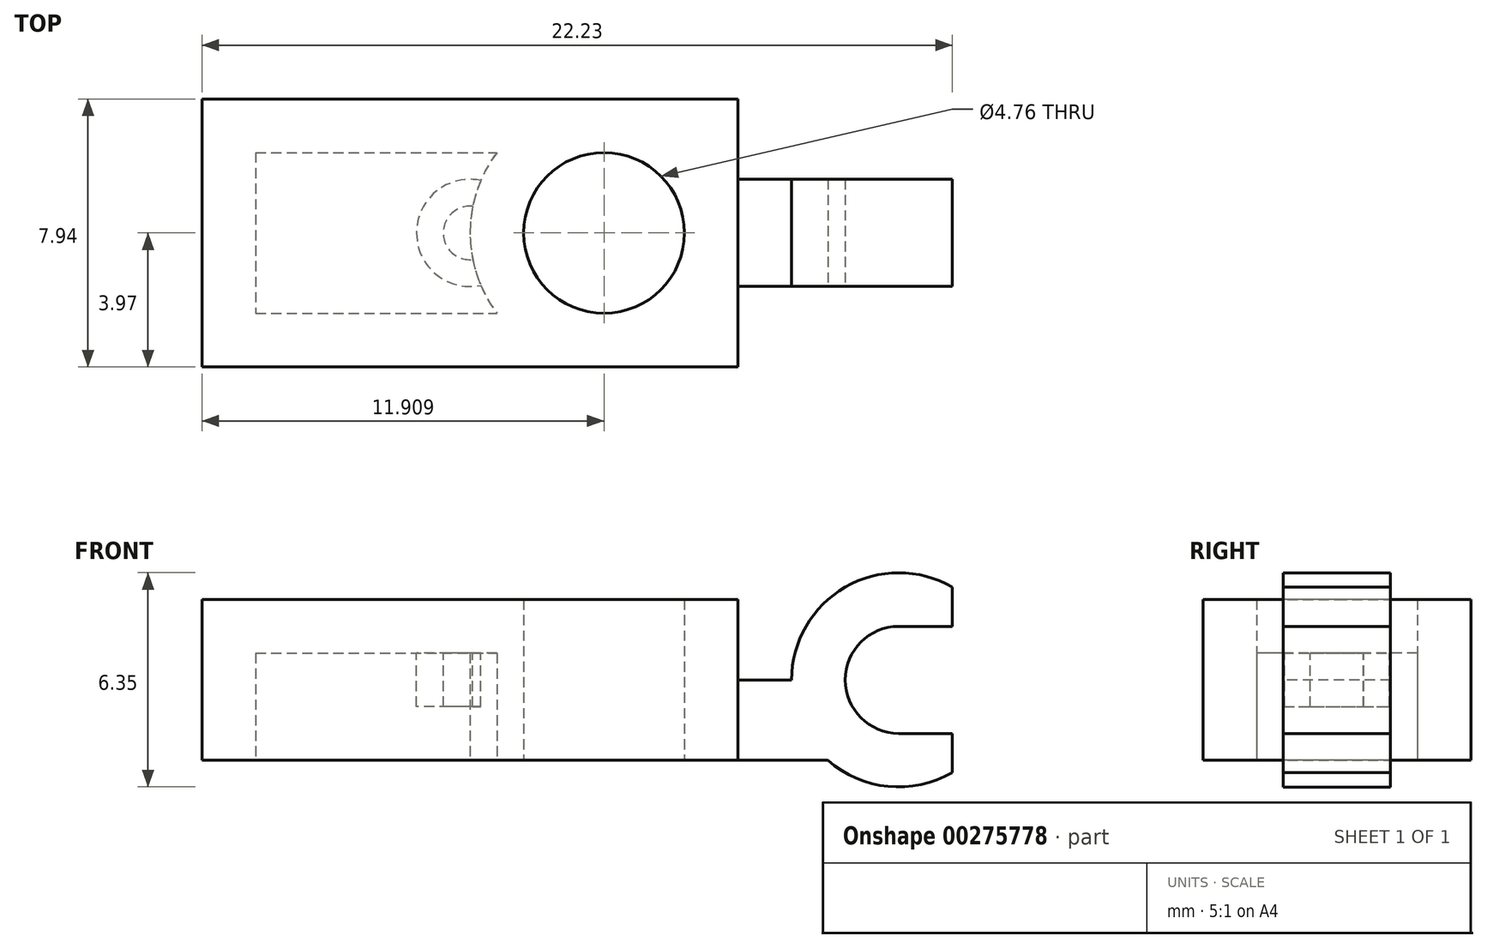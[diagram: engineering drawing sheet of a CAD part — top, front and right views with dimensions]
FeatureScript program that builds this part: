
annotation { "Feature Type Name" : "Feature", "Feature Type Description" : "" }
export const myFeature = defineFeature(function(context is Context, id is Id, definition is map)
    precondition{}
    {
        {
            var Q0;
            Q0=qCreatedBy(makeId("Top.planeOp"),FACE);
            var sketch = newSketch(context, id + "F0", { "sketchPlane" : qUnion([Q0])});
            skLineSegment(sketch, "E0.bottom", {"start": v(-7.94, 3.97) * mm, "end": v(7.94, 3.97) * mm});
            skLineSegment(sketch, "E0.top", {"start": v(-7.94, -3.97) * mm, "end": v(7.94, -3.97) * mm});
            skLineSegment(sketch, "E0.left", {"start": v(-7.94, 3.97) * mm, "end": v(-7.94, -3.97) * mm});
            skLineSegment(sketch, "E0.right", {"start": v(7.94, 3.97) * mm, "end": v(7.94, -3.97) * mm});
            skPoint(sketch, "E0.middle", {"position": v(0, 0) * mm});
            skCircle(sketch, "E1", {"center": v(-3.97, 0) * mm, "radius": 2.38 * mm});
            skCircle(sketch, "E2.MirrorC", {"center": v(3.97, 0) * mm, "radius": 2.38 * mm});
            skSolve(sketch);
        }
        {
            var Q0;
            Q0=makeQuery(id+"F0.imprint","IMPRINT",FACE,{"disambiguationData":[TD([[makeQuery(id+"F0.imprint","IMPRINT",EDGE,{"derivedFrom":sQuery(id+"F0.wireOp",EDGE,"E0.bottom")}),-1.0]])]});
            extrude(context, id + "F1", {"entities" : qUnion([Q0]), "depth" : 3.17 * mm});
        }
        {
            var Q0;
            Q0=makeQuery(id+"F0.imprint","IMPRINT",FACE,{"disambiguationData":[TD([[makeQuery(id+"F0.imprint","IMPRINT",EDGE,{"derivedFrom":sQuery(id+"F0.wireOp",EDGE,"E2.MirrorC")}),-1.0]])]});
            var Q1;
            Q1=makeQuery(id+"F0.imprint","IMPRINT",FACE,{"disambiguationData":[TD([[makeQuery(id+"F0.imprint","IMPRINT",EDGE,{"derivedFrom":sQuery(id+"F0.wireOp",EDGE,"E1")}),1.0]])]});
            extrude(context, id + "F2", {"entities" : qUnion([Q0, Q1]), "operationType" : NewBodyOperationType.ADD, "depth" : 4.76 * mm});
        }
        {
            var Q0;
            {var subQ0=sQuery(id+"F0.wireOp",EDGE,"E2.MirrorC");var subQ1=sQuery(id+"F0.wireOp",EDGE,"E1");Q0=makeQuery(id+"F2.boolean.opBoolean","MERGE",FACE,{"derivedFrom":[makeQuery(id+"F1.opExtrude","CAP_FACE",FACE,{"disambiguationData":[OSD([sQuery(id+"F0.wireOp",EDGE,"E0.bottom"),sQuery(id+"F0.wireOp",EDGE,"E0.top"),sQuery(id+"F0.wireOp",EDGE,"E0.left"),sQuery(id+"F0.wireOp",EDGE,"E0.right"),subQ1,subQ0])],"isStart":true}),makeQuery(id+"F2.opExtrude","CAP_FACE",FACE,{"disambiguationData":[OSD([subQ1])],"isStart":true}),makeQuery(id+"F2.opExtrude","CAP_FACE",FACE,{"disambiguationData":[OSD([subQ0])],"isStart":true})]});}
            shell(context, id + "F3", {"entities" : qUnion([Q0]), "thickness" : 1.59 * mm});
        }
        {
            var Q0;
            Q0=makeQuery(id+"F3.opShell","OFFSET_FACE",FACE,{"disambiguationData":[OSD([sQuery(id+"F0.wireOp",EDGE,"E0.bottom"),sQuery(id+"F0.wireOp",EDGE,"E0.top"),sQuery(id+"F0.wireOp",EDGE,"E0.left"),sQuery(id+"F0.wireOp",EDGE,"E0.right"),sQuery(id+"F0.wireOp",EDGE,"E1"),sQuery(id+"F0.wireOp",EDGE,"E2.MirrorC")])]});
            var sketch = newSketch(context, id + "F4", { "sketchPlane" : qUnion([Q0])});
            skCircle(sketch, "E3", {"center": v(0, 0) * mm, "radius": 1.59 * mm});
            skCircle(sketch, "E4", {"center": v(0, 0) * mm, "radius": 0.8 * mm});
            skSolve(sketch);
        }
        {
            var Q0;
            Q0=makeQuery(id+"F4.imprint","IMPRINT",FACE,{"disambiguationData":[TD([[makeQuery(id+"F4.imprint","IMPRINT",EDGE,{"derivedFrom":sQuery(id+"F4.wireOp",EDGE,"E3")}),1.0]])]});
            extrude(context, id + "F5", {"entities" : qUnion([Q0]), "operationType" : NewBodyOperationType.ADD, "depth" : 1.59 * mm});
        }
        {
            var Q0;
            Q0=makeQuery(id+"F1.opExtrude","SWEPT_FACE",FACE,{"disambiguationData":[OSD([sQuery(id+"F0.wireOp",EDGE,"E0.right")])]});
            var sketch = newSketch(context, id + "F6", { "sketchPlane" : qUnion([Q0])});
            skLineSegment(sketch, "E5", {"start": v(0, 0) * mm, "end": v(1.59, 0) * mm});
            skLineSegment(sketch, "E6", {"start": v(1.59, 0) * mm, "end": v(1.59, 6.35) * mm});
            skLineSegment(sketch, "E7", {"start": v(1.59, 6.35) * mm, "end": v(0, 6.35) * mm});
            skLineSegment(sketch, "E8", {"start": v(0, 6.35) * mm, "end": v(0, 0) * mm});
            skLineSegment(sketch, "E9.MirrorCS", {"start": v(-1.59, 6.35) * mm, "end": v(0, 6.35) * mm});
            skLineSegment(sketch, "E10.MirrorCS", {"start": v(-1.59, 0) * mm, "end": v(-1.59, 6.35) * mm});
            skLineSegment(sketch, "E11.MirrorCS", {"start": v(0, 0) * mm, "end": v(-1.59, 0) * mm});
            skSolve(sketch);
        }
        {
            var Q0;
            Q0=qSketchRegion(id+"F6",true);
            extrude(context, id + "F7", {"entities" : qUnion([Q0]), "operationType" : NewBodyOperationType.ADD, "depth" : 4.76 * mm});
        }
        {
            var Q0;
            Q0=makeQuery(id+"F7.opExtrude","SWEPT_FACE",FACE,{"disambiguationData":[OSD([sQuery(id+"F6.wireOp",EDGE,"E10.MirrorCS")])]});
            var sketch = newSketch(context, id + "F8", { "sketchPlane" : qUnion([Q0])});
            skLineSegment(sketch, "E12", {"start": v(7.94, 3.17) * mm, "end": v(7.94, 2.38) * mm});
            skLineSegment(sketch, "E13", {"start": v(7.94, 2.38) * mm, "end": v(9.53, 2.38) * mm});
            skLineSegment(sketch, "E14", {"start": v(9.53, 2.38) * mm, "end": v(12.7, 2.38) * mm});
            skCircle(sketch, "E15", {"center": v(12.7, 2.38) * mm, "radius": 3.17 * mm});
            skCircle(sketch, "E16.0", {"center": v(12.7, 2.38) * mm, "radius": 1.59 * mm});
            skLineSegment(sketch, "E17", {"start": v(12.7, 0) * mm, "end": v(12.7, -0.8) * mm});
            skLineSegment(sketch, "E18", {"start": v(12.7, 0) * mm, "end": v(14.29, 0) * mm});
            skLineSegment(sketch, "E19", {"start": v(14.29, 0) * mm, "end": v(14.29, -0.37) * mm});
            skLineSegment(sketch, "E20", {"start": v(14.29, -0.37) * mm, "end": v(14.29, 5.13) * mm});
            skLineSegment(sketch, "E21", {"start": v(12.7, 0.8) * mm, "end": v(14.29, 0.8) * mm});
            skLineSegment(sketch, "E22", {"start": v(12.7, 3.97) * mm, "end": v(14.29, 3.97) * mm});
            skSolve(sketch);
        }
        {
            var Q0;
            {var subQ0=sQuery(id+"F8.wireOp",EDGE,"E17");Q0=makeQuery(id+"F8.imprint","IMPRINT",FACE,{"disambiguationData":[TD([[makeQuery(id+"F8.imprint","IMPRINT",EDGE,{"derivedFrom":subQ0}),-1.0]])]});}
            var Q1;
            {var subQ0=sQuery(id+"F8.wireOp",EDGE,"E17");Q1=makeQuery(id+"F8.imprint","IMPRINT",FACE,{"disambiguationData":[TD([[makeQuery(id+"F8.imprint","IMPRINT",EDGE,{"derivedFrom":subQ0}),1.0]])]});}
            var Q2;
            {var subQ5=sQuery(id+"F8.wireOp",EDGE,"E22");Q2=makeQuery(id+"F8.imprint","IMPRINT",FACE,{"disambiguationData":[TD([[makeQuery(id+"F8.imprint","IMPRINT",EDGE,{"derivedFrom":subQ5}),1.0]])]});}
            var Q3;
            {var subQ0=sQuery(id+"F8.wireOp",EDGE,"E18");Q3=makeQuery(id+"F8.imprint","IMPRINT",FACE,{"disambiguationData":[TD([[makeQuery(id+"F8.imprint","IMPRINT",EDGE,{"derivedFrom":subQ0}),1.0]])]});}
            extrude(context, id + "F9", {"entities" : qUnion([Q0, Q1, Q2, Q3]), "operationType" : NewBodyOperationType.ADD, "oppositeDirection" : true, "depth" : 3.17 * mm});
        }
        {
            var Q0;
            Q0=makeQuery(id+"F8.imprint","IMPRINT",FACE,{"disambiguationData":[TD([[makeQuery(id+"F8.imprint","IMPRINT",EDGE,{"derivedFrom":sQuery(id+"F8.wireOp",EDGE,"E12")}),-1.0]])]});
            var Q1;
            {var subQ0=sQuery(id+"F8.wireOp",EDGE,"E14");var subQ1=makeQuery(id+"F7.opExtrude","CAP_EDGE",EDGE,{"disambiguationData":[OSD([sQuery(id+"F6.wireOp",EDGE,"E10.MirrorCS")])],"isStart":false});var subQ2=makeQuery(id+"F8.imprint","INTERSECT",VERTEX,{"derivedFrom":[subQ1,subQ0]});Q1=makeQuery(id+"F8.imprint","IMPRINT",FACE,{"disambiguationData":[TD([[makeQuery(id+"F8.imprint","IMPRINT",EDGE,{"disambiguationData":[TD([[subQ2,1.0]])],"derivedFrom":subQ0}),-1.0]])]});}
            var Q2;
            {var subQ0=sQuery(id+"F8.wireOp",EDGE,"E14");var subQ1=makeQuery(id+"F7.opExtrude","CAP_EDGE",EDGE,{"disambiguationData":[OSD([sQuery(id+"F6.wireOp",EDGE,"E10.MirrorCS")])],"isStart":false});var subQ2=makeQuery(id+"F8.imprint","INTERSECT",VERTEX,{"derivedFrom":[subQ1,subQ0]});Q2=makeQuery(id+"F8.imprint","IMPRINT",FACE,{"disambiguationData":[TD([[makeQuery(id+"F8.imprint","IMPRINT",EDGE,{"disambiguationData":[TD([[subQ2,1.0]])],"derivedFrom":subQ0}),1.0]])]});}
            extrude(context, id + "F10", {"entities" : qUnion([Q0, Q1, Q2]), "operationType" : NewBodyOperationType.REMOVE, "oppositeDirection" : true, "depth" : 25.4 * mm});
        }
    });
